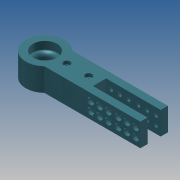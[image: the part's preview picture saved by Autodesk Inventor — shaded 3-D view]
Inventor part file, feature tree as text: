
AUTODESK INVENTOR PART (.ipt)
format: ipt  version: 2013 (Build 170138000, 138)  size: 291,840 bytes
history: native  units: mm
features: extrude x9, sketch x9, fillet x2, pattern_linear x2
ambient origin geometry x8: Origin, YZ Plane, XZ Plane, XY Plane, X Axis, Y Axis, Z Axis, Center Point
bodies: Solid1 (feature_tree)
feature tree (22):
  extrude  "Extrusion1"  Depth=12.6mm
  extrude  "Extrusion2"  Depth=8.5mm
  extrude  "Extrusion5"  Depth=22.0mm
  extrude  "Extrusion6"  Depth=35.0mm
  fillet  "Fillet1"  Radius=10.0mm
  extrude  "Extrusion7"  Depth=8.0mm TaperAngle=0.0deg
  extrude  "Extrusion8"  Depth=12.0mm
  extrude  "Extrusion9"  Depth=50.0mm
  extrude  "Extrusion10"  Depth=12.5mm
  pattern_linear  "Rectangular Pattern1"  Spacing1=3.5mm  [1 undecoded]
  pattern_linear  "Rectangular Pattern2"  Spacing1=10.0mm  [1 undecoded]
  extrude  "Extrusion11"  Depth=6.0mm
  fillet  "Fillet2"  Radius=3.0mm
  sketch  "Sketch1"  dims[d0=150.0mm d2=12.6mm]
  sketch  "Sketch2"  dims[d3=15.0mm d4=8.5mm]
  sketch  "Sketch6"  dims[d5=21.1mm d6=0.0mm d7=22.0mm]
  sketch  "Sketch7"  dims[d9=7.0mm d10=0.0mm d24=35.0mm d26=10.0mm d27=0.0mm]
  sketch  "Sketch8"  dims[d30=14.0mm d32=8.0mm d33=0.0mm]
  sketch  "Sketch9"  dims[d34=3.5mm d35=12.0mm]
  sketch  "Sketch10"  dims[d37=50.0mm d38=50.0mm]
  sketch  "Sketch11"  dims[d39=10.0mm d40=0.0mm d41=12.5mm]
  sketch  "Sketch12"  dims[d42=8.0mm d43=3.5mm d44=10.0mm d45=0.0mm d46=6.0mm d48=3.0mm d49=0.0mm d50=5.5mm d51=4.0mm d52=0.0mm d53=30.0mm d55=8.0mm d56=20.0mm d58=8.0mm d59=20.0mm d61=25.0mm d62=7.0mm d63=0.0mm d64=3.5mm]
note: 2 required parameter values undecoded (feature->parameter linkage not recoverable at this tier; creation-order binding heuristic only, values carry confidence <= 0.55)
